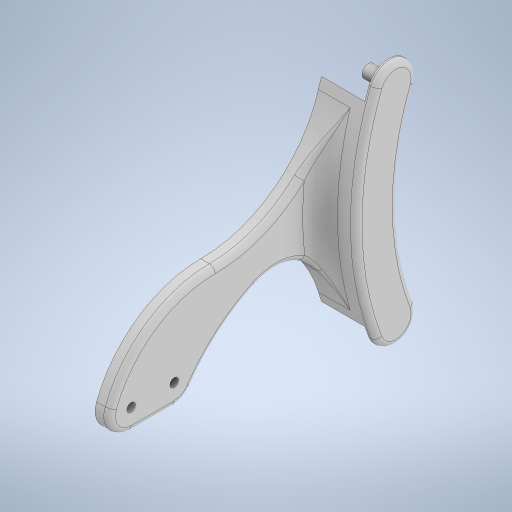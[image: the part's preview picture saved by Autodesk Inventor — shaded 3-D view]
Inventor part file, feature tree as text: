
AUTODESK INVENTOR PART (.ipt)
format: ipt  version: 2023 (Build 270158000, 158)  size: 375,296 bytes
history: native  units: mm
features: extrude x4, other x3, sketch x1, fillet x1
ambient origin geometry x8: Origin, YZ Plane, XZ Plane, XY Plane, X Axis, Y Axis, Z Axis, Center Point
bodies: Body1 (feature_tree)
feature tree (9):
  other  "Sólido1"
  sketch  "Boceto1"  dims[d0=100.0mm d1=85.0mm d2=70.5mm d3=7.25mm d4=7.25mm d5=14.9mm d6=15.0mm d7=157.0mm d8=4.5mm d9=7.0mm d10=0.0mm d11=8.0mm d12=2.5mm d13=0.0mm d14=1.0mm d17=10.0mm d18=10.0mm d19=23.0mm d20=10.0mm d22=3.0mm d23=110.0mm d24=15.0mm d25=0.0mm d26=10.0mm d27=0.0mm d28=17.0mm d29=6.0mm d30=2.0mm]
  extrude  "Extrusión1"  Depth=85.0mm
  extrude  "Extrusión2"  Depth=70.5mm
  extrude  "Extrusión4"  Depth=7.25mm
  extrude  "Extrusión5"  Depth=7.25mm
  other  "Empalme de cara1"
  other  "Empalme de cara2"
  fillet  "Empalme1"  Radius=14.9mm
